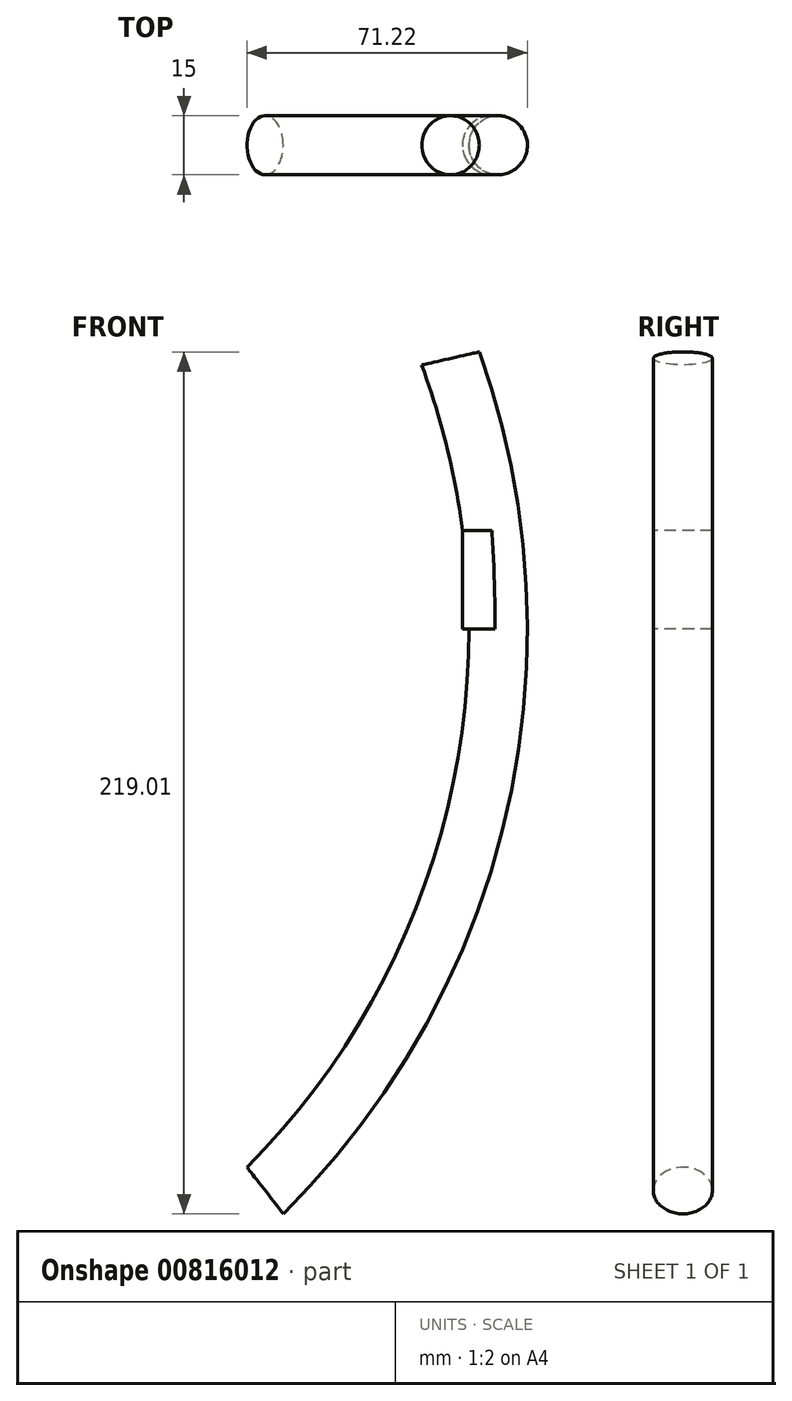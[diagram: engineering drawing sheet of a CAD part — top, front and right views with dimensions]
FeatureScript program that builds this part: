
annotation { "Feature Type Name" : "Feature", "Feature Type Description" : "" }
export const myFeature = defineFeature(function(context is Context, id is Id, definition is map)
    precondition{}
    {
        {
            var Q0;
            Q0=qCreatedBy(makeId("Front.planeOp"),FACE);
            var sketch = newSketch(context, id + "F0", { "sketchPlane" : qUnion([Q0])});
            skArc(sketch, "E0", {"start": v(141.42, -141.42) * mm, "mid": v(195.26, -43.29) * mm, "end": v(187.94, 68.4) * mm});
            skPoint(sketch, "E1.end.orphan", {"position": v(205.06, -205.06) * mm});
            skPoint(sketch, "E2.end.orphan", {"position": v(281.9, 102.6) * mm});
            skSolve(sketch);
        }
        {
            var Q0;
            Q0=qCreatedBy(makeId("Top.planeOp"),FACE);
            var sketch = newSketch(context, id + "F1", { "sketchPlane" : qUnion([Q0])});
            skCircle(sketch, "E3", {"center": v(200, 0) * mm, "radius": 7.5 * mm});
            skSolve(sketch);
        }
        {
            var Q0;
            Q0 = qSketchRegion(id + "F1", true);
            extrude(context, id + "F2", {"entities" : qUnion([Q0]), "depth" : 25 * mm, "offsetDistance" : 25 * mm});
        }
        {
            var Q0;
            Q0=makeQuery(id+"F2.opExtrude","CAP_FACE",FACE,{"disambiguationData":[OSD([sQuery(id+"F1.wireOp",EDGE,"E3")])],"isStart":false});
            var Q1;
            Q1=sQuery(id+"F0.wireOp",EDGE,"E0");
            sweep(context, id + "F3", {"operationType" : NewBodyOperationType.ADD, "profiles" : qUnion([Q0]), "path" : qUnion([Q1])});
        }
    });
